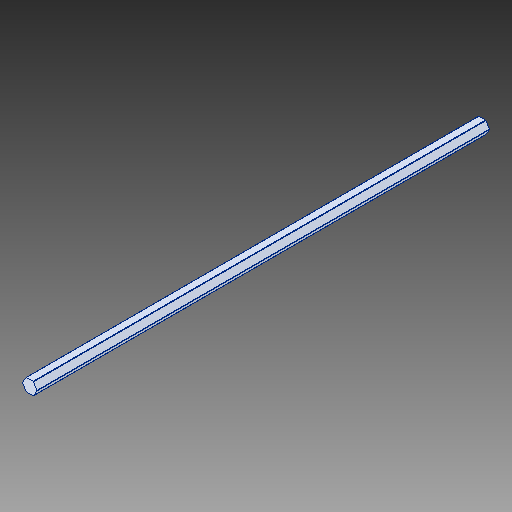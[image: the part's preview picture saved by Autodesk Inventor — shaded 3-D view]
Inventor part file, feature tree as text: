
AUTODESK INVENTOR PART (.ipt)
format: ipt  version: 2017 (Build 210142000, 142)  size: 97,792 bytes
history: native  units: in
note: dims shown in document units (in); Inventor stores cm internally (conversion verified against a paired STEP export)
features: fillet x1
ambient origin geometry x8: Origin, YZ Plane, XZ Plane, XY Plane, X Axis, Y Axis, Z Axis, Center Point
bodies: Solid1 (feature_tree)
feature tree (1):
  fillet  "Fillet1"  [1 undecoded]
note: 1 required parameter value undecoded (feature->parameter linkage not recoverable at this tier; creation-order binding heuristic only, values carry confidence <= 0.55)
